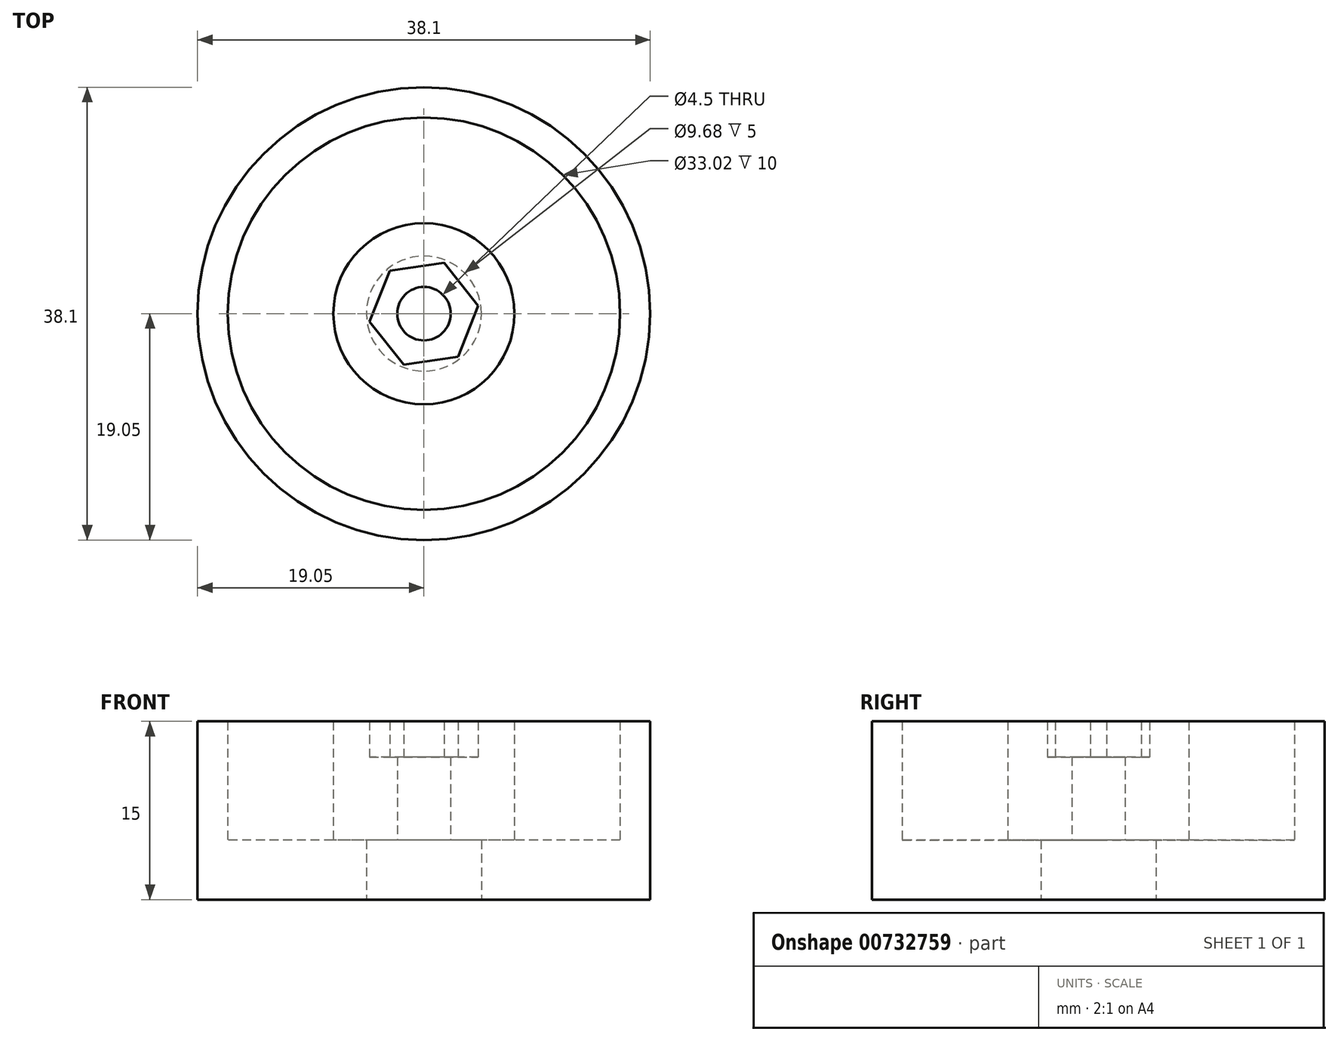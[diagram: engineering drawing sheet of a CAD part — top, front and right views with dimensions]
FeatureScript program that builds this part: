
annotation { "Feature Type Name" : "Feature", "Feature Type Description" : "" }
export const myFeature = defineFeature(function(context is Context, id is Id, definition is map)
    precondition{}
    {
        {
            var Q0;
            Q0=qCreatedBy(makeId("Top.planeOp"),FACE);
            var sketch = newSketch(context, id + "F0", { "sketchPlane" : qUnion([Q0])});
            skCircle(sketch, "E0", {"center": v(0, 0) * mm, "radius": 19.05 * mm});
            skCircle(sketch, "E1", {"center": v(0, 0) * mm, "radius": 2.25 * mm});
            skCircle(sketch, "E2", {"center": v(0, 0) * mm, "radius": 16.51 * mm});
            skCircle(sketch, "E3.cCircle", {"center": v(0, 0) * mm, "radius": 4 * mm, "construction": true});
            skLineSegment(sketch, "E3.0", {"start": v(1.7, 4.3) * mm, "end": v(4.57, 0.67) * mm});
            skLineSegment(sketch, "E3.1", {"start": v(4.57, 0.67) * mm, "end": v(2.87, -3.62) * mm});
            skLineSegment(sketch, "E3.2", {"start": v(2.87, -3.62) * mm, "end": v(-1.7, -4.3) * mm});
            skLineSegment(sketch, "E3.3", {"start": v(-1.7, -4.3) * mm, "end": v(-4.57, -0.67) * mm});
            skLineSegment(sketch, "E3.4", {"start": v(-4.57, -0.67) * mm, "end": v(-2.87, 3.62) * mm});
            skLineSegment(sketch, "E3.5", {"start": v(-2.87, 3.62) * mm, "end": v(1.7, 4.3) * mm});
            skPoint(sketch, "E3.0.midPoint", {"position": v(3.14, 2.48) * mm});
            skCircle(sketch, "E4", {"center": v(0, 0) * mm, "radius": 7.62 * mm});
            skCircle(sketch, "E5", {"center": v(0, 0) * mm, "radius": 4.84 * mm});
            skSolve(sketch);
        }
        {
            var Q0;
            Q0=makeQuery(id+"F0.imprint","IMPRINT",FACE,{"disambiguationData":[TD([[makeQuery(id+"F0.imprint","IMPRINT",EDGE,{"derivedFrom":sQuery(id+"F0.wireOp",EDGE,"E0")}),1.0]])]});
            var Q1;
            Q1=makeQuery(id+"F0.imprint","IMPRINT",FACE,{"disambiguationData":[TD([[makeQuery(id+"F0.imprint","IMPRINT",EDGE,{"derivedFrom":sQuery(id+"F0.wireOp",EDGE,"E2")}),1.0]])]});
            var Q2;
            Q2=makeQuery(id+"F0.imprint","IMPRINT",FACE,{"disambiguationData":[TD([[makeQuery(id+"F0.imprint","IMPRINT",EDGE,{"derivedFrom":sQuery(id+"F0.wireOp",EDGE,"E4")}),1.0]])]});
            extrude(context, id + "F1", {"entities" : qUnion([Q0, Q1, Q2]), "depth" : 5 * mm, "offsetDistance" : 25.4 * mm});
        }
        {
            var Q0;
            Q0=makeQuery(id+"F0.imprint","IMPRINT",FACE,{"disambiguationData":[TD([[makeQuery(id+"F0.imprint","IMPRINT",EDGE,{"derivedFrom":sQuery(id+"F0.wireOp",EDGE,"E0")}),1.0]])]});
            var Q1;
            Q1=makeQuery(id+"F0.imprint","IMPRINT",FACE,{"disambiguationData":[TD([[makeQuery(id+"F0.imprint","IMPRINT",EDGE,{"derivedFrom":sQuery(id+"F0.wireOp",EDGE,"E3.0")}),1.0]])]});
            var Q2;
            Q2=makeQuery(id+"F0.imprint","IMPRINT",FACE,{"disambiguationData":[TD([[makeQuery(id+"F0.imprint","IMPRINT",EDGE,{"derivedFrom":sQuery(id+"F0.wireOp",EDGE,"E1")}),-1.0]])]});
            var Q3;
            Q3=makeQuery(id+"F0.imprint","IMPRINT",FACE,{"disambiguationData":[TD([[makeQuery(id+"F0.imprint","IMPRINT",EDGE,{"derivedFrom":sQuery(id+"F0.wireOp",EDGE,"E4")}),1.0]])]});
            extrude(context, id + "F2", {"entities" : qUnion([Q0, Q1, Q2, Q3]), "operationType" : NewBodyOperationType.ADD, "depth" : 15 * mm, "offsetDistance" : 25.4 * mm, "hasSecondDirection" : true, "secondDirectionOppositeDirection" : false, "secondDirectionDepth" : 5 * mm});
        }
        {
            var Q0;
            Q0=makeQuery(id+"F0.imprint","IMPRINT",FACE,{"disambiguationData":[TD([[makeQuery(id+"F0.imprint","IMPRINT",EDGE,{"derivedFrom":sQuery(id+"F0.wireOp",EDGE,"E1")}),-1.0]])]});
            extrude(context, id + "F3", {"entities" : qUnion([Q0]), "operationType" : NewBodyOperationType.REMOVE, "depth" : 20 * mm, "offsetDistance" : 25.4 * mm, "hasSecondDirection" : true, "secondDirectionOppositeDirection" : false, "secondDirectionDepth" : 12 * mm});
        }
    });
